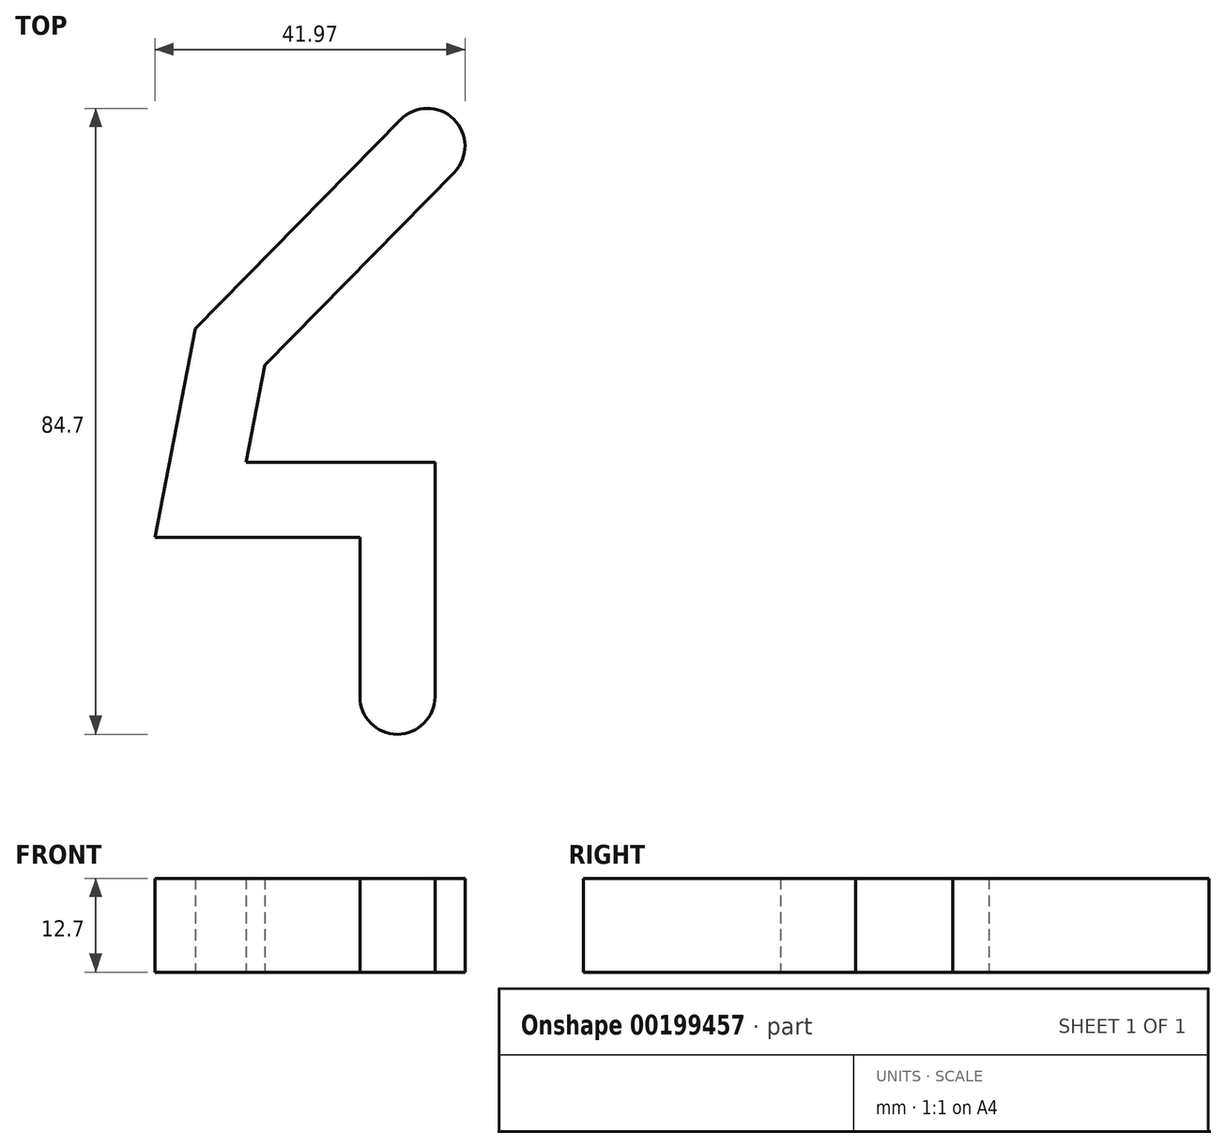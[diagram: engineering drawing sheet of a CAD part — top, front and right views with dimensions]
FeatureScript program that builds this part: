
annotation { "Feature Type Name" : "Feature", "Feature Type Description" : "" }
export const myFeature = defineFeature(function(context is Context, id is Id, definition is map)
    precondition{}
    {
        {
            var Q0;
            Q0=qCreatedBy(makeId("Top.planeOp"),FACE);
            var sketch = newSketch(context, id + "F0", { "sketchPlane" : qUnion([Q0])});
            skLineSegment(sketch, "E0", {"start": v(0, 0) * mm, "end": v(0, 26.67) * mm});
            skLineSegment(sketch, "E1", {"start": v(0, 26.67) * mm, "end": v(-26.67, 26.67) * mm});
            skLineSegment(sketch, "E2", {"start": v(-26.67, 26.67) * mm, "end": v(-22.65, 47.36) * mm});
            skLineSegment(sketch, "E3", {"start": v(-22.65, 47.36) * mm, "end": v(4.06, 74.54) * mm});
            skLineSegment(sketch, "E4.0", {"start": v(-17.95, 44.9) * mm, "end": v(7.68, 70.98) * mm});
            skLineSegment(sketch, "E4.1", {"start": v(-20.5, 31.75) * mm, "end": v(-17.95, 44.9) * mm});
            skLineSegment(sketch, "E4.2", {"start": v(5.08, 31.75) * mm, "end": v(-20.5, 31.75) * mm});
            skLineSegment(sketch, "E4.3", {"start": v(5.08, 0) * mm, "end": v(5.08, 31.75) * mm});
            skLineSegment(sketch, "E5.0", {"start": v(-27.34, 49.83) * mm, "end": v(0.43, 78.1) * mm});
            skLineSegment(sketch, "E5.1", {"start": v(-32.83, 21.59) * mm, "end": v(-27.34, 49.83) * mm});
            skLineSegment(sketch, "E5.2", {"start": v(-5.08, 21.59) * mm, "end": v(-32.83, 21.59) * mm});
            skLineSegment(sketch, "E5.3", {"start": v(-5.08, 0) * mm, "end": v(-5.08, 21.59) * mm});
            skArc(sketch, "E6", {"start": v(7.68, 70.98) * mm, "mid": v(7.62, 78.16) * mm, "end": v(0.43, 78.1) * mm});
            skArc(sketch, "E7", {"start": v(-5.08, 0) * mm, "mid": v(0, -5.08) * mm, "end": v(5.08, 0) * mm});
            skSolve(sketch);
        }
        {
            var Q0;
            Q0=qCreatedBy(makeId("Right.planeOp"),FACE);
            var sketch = newSketch(context, id + "F1", { "sketchPlane" : qUnion([Q0])});
            skLineSegment(sketch, "E8", {"start": v(-5.08, 0) * mm, "end": v(0, 0) * mm});
            skLineSegment(sketch, "E9", {"start": v(0, 0) * mm, "end": v(10.16, 0) * mm});
            skLineSegment(sketch, "E10", {"start": v(10.16, 0) * mm, "end": v(16.5, 6.35) * mm});
            skLineSegment(sketch, "E11", {"start": v(16.5, 6.35) * mm, "end": v(90.54, 6.35) * mm});
            skLineSegment(sketch, "E12", {"start": v(90.54, 6.35) * mm, "end": v(90.54, 12.7) * mm});
            skLineSegment(sketch, "E13", {"start": v(90.54, 12.7) * mm, "end": v(13.88, 12.7) * mm});
            skLineSegment(sketch, "E14", {"start": v(13.88, 12.7) * mm, "end": v(7.53, 6.35) * mm});
            skLineSegment(sketch, "E15", {"start": v(7.53, 6.35) * mm, "end": v(-5.08, 6.35) * mm});
            skLineSegment(sketch, "E16", {"start": v(-5.08, 6.35) * mm, "end": v(-5.08, 0) * mm});
            skSolve(sketch);
        }
        {
            var Q0;
            Q0 = qSketchRegion(id + "F0", true);
            var Q1;
            Q1=sQuery(id+"F1.wireOp",VERTEX,"E13.start");
            extrude(context, id + "F2", {"entities" : qUnion([Q0]), "endBound" : BoundingType.UP_TO_VERTEX, "endBoundEntityVertex" : qUnion([Q1]), "depth" : 12.7 * mm});
        }
    });
